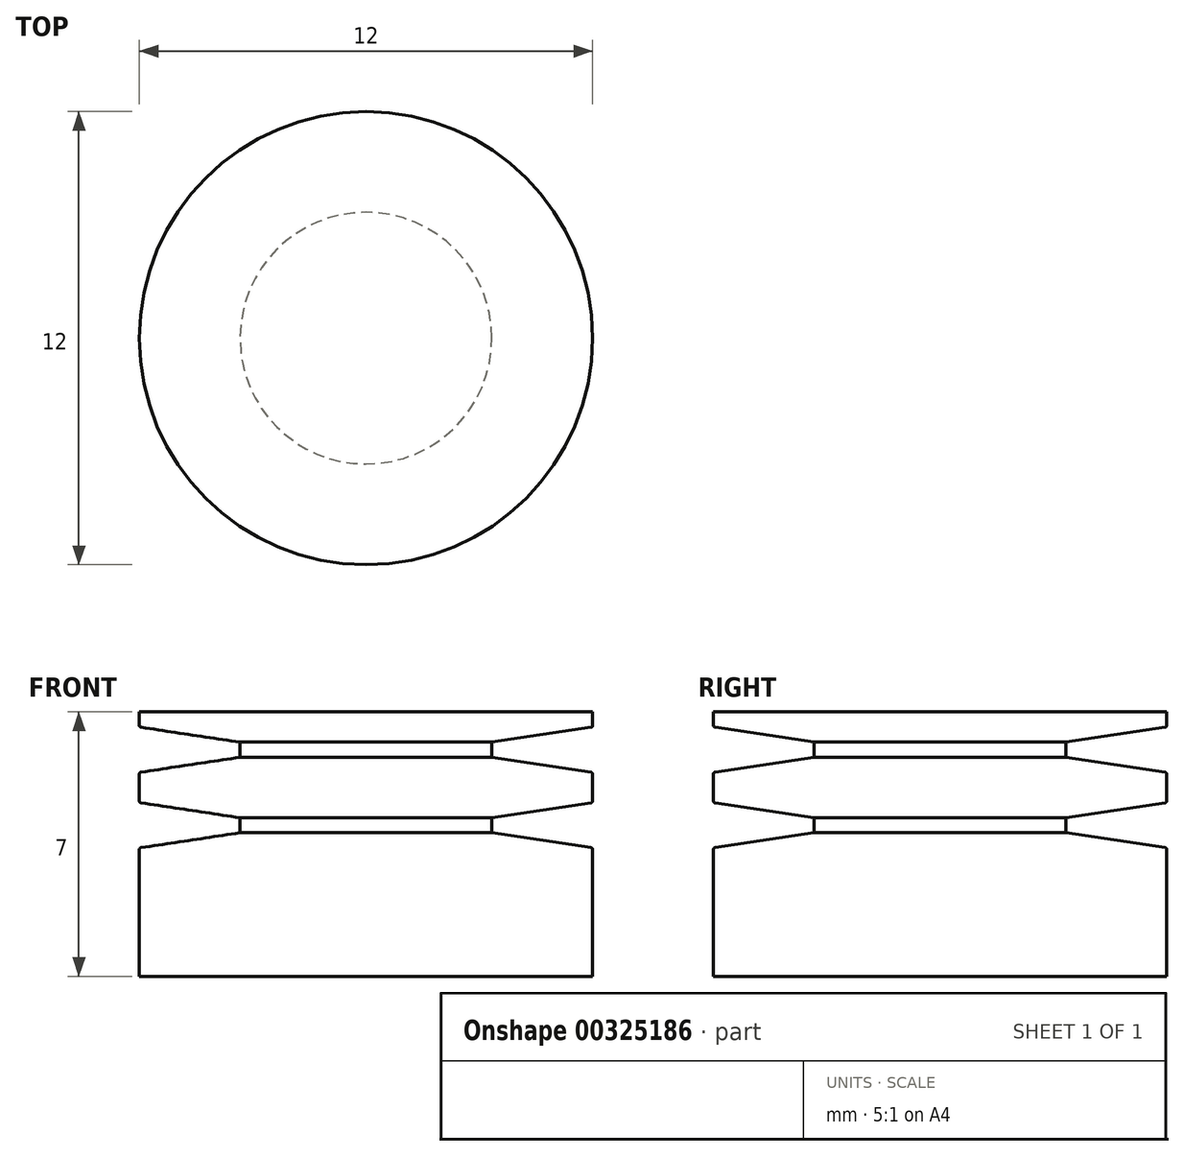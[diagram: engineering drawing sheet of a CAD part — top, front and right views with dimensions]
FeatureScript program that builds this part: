
annotation { "Feature Type Name" : "Feature", "Feature Type Description" : "" }
export const myFeature = defineFeature(function(context is Context, id is Id, definition is map)
    precondition{}
    {
        {
            var Q0;
            Q0=qCreatedBy(makeId("Front.planeOp"),FACE);
            var sketch = newSketch(context, id + "F0", { "sketchPlane" : qUnion([Q0])});
            skLineSegment(sketch, "E0.top", {"start": v(0, 3) * mm, "end": v(6, 3) * mm});
            skLineSegment(sketch, "E1", {"start": v(0, 3) * mm, "end": v(0, 4) * mm});
            skLineSegment(sketch, "E2", {"start": v(0, 4) * mm, "end": v(2, 4) * mm});
            skLineSegment(sketch, "E3", {"start": v(6, 3) * mm, "end": v(6, 3.36) * mm});
            skLineSegment(sketch, "E4", {"start": v(5.96, 3.4) * mm, "end": v(2, 4) * mm});
            skLineSegment(sketch, "E5", {"start": v(3.33, 4) * mm, "end": v(3.33, 3.8) * mm});
            skLineSegment(sketch, "E6", {"start": v(2, 4) * mm, "end": v(3.33, 4) * mm});
            skPoint(sketch, "E7.visualSharp", {"position": v(6, 3.4) * mm});
            skArc(sketch, "E7.filletArc", {"start": v(6, 3.36) * mm, "mid": v(5.99, 3.39) * mm, "end": v(5.96, 3.4) * mm});
            skSolve(sketch);
        }
        {
            var Q0;
            Q0=makeQuery(id+"F0.imprint","IMPRINT",FACE,{"disambiguationData":[TD([[makeQuery(id+"F0.imprint","IMPRINT",EDGE,{"derivedFrom":sQuery(id+"F0.wireOp",EDGE,"E0.top")}),1.0]])]});
            var Q1;
            {var subQ2=sQuery(id+"F0.wireOp",EDGE,"E5");Q1=makeQuery(id+"F0.imprint","IMPRINT",FACE,{"disambiguationData":[TD([[makeQuery(id+"F0.imprint","IMPRINT",EDGE,{"derivedFrom":subQ2}),-1.0]])]});}
            var Q2;
            Q2=sQuery(id+"F0.wireOp",EDGE,"E1");
            revolve(context, id + "F1", {"entities" : qUnion([Q0, Q1]), "axis" : qUnion([Q2]), "revolveType" : RevolveType.FULL});
        }
        {
            var Q0;
            Q0=makeQuery(id+"F1.opRevolve","SWEPT_BODY",BODY,{"disambiguationData":[OSD([sQuery(id+"F0.wireOp",EDGE,"E0.top"),sQuery(id+"F0.wireOp",EDGE,"E1"),sQuery(id+"F0.wireOp",EDGE,"E2"),sQuery(id+"F0.wireOp",EDGE,"E3"),sQuery(id+"F0.wireOp",EDGE,"E4"),sQuery(id+"F0.wireOp",EDGE,"E5"),sQuery(id+"F0.wireOp",EDGE,"E6")])]});
            var Q1;
            Q1=makeQuery(id+"F1.opRevolve","SWEPT_FACE",FACE,{"disambiguationData":[OSD([sQuery(id+"F0.wireOp",EDGE,"E2"),sQuery(id+"F0.wireOp",EDGE,"E6")])]});
            mirror(context, id + "F2", {"operationType" : NewBodyOperationType.ADD, "entities" : qUnion([Q0]), "mirrorPlane" : qUnion([Q1])});
        }
        {
            var Q0;
            Q0=makeQuery(id+"F1.opRevolve","SWEPT_BODY",BODY,{"disambiguationData":[OSD([sQuery(id+"F0.wireOp",EDGE,"E0.top"),sQuery(id+"F0.wireOp",EDGE,"E1"),sQuery(id+"F0.wireOp",EDGE,"E2"),sQuery(id+"F0.wireOp",EDGE,"E3"),sQuery(id+"F0.wireOp",EDGE,"E4"),sQuery(id+"F0.wireOp",EDGE,"E5"),sQuery(id+"F0.wireOp",EDGE,"E6")])]});
            var Q1;
            Q1=makeQuery(id+"F2.opPattern","COPY",FACE,{"derivedFrom":makeQuery(id+"F1.opRevolve","SWEPT_FACE",FACE,{"disambiguationData":[OSD([sQuery(id+"F0.wireOp",EDGE,"E0.top")])]}),"instanceName":"1"});
            mirror(context, id + "F3", {"operationType" : NewBodyOperationType.ADD, "entities" : qUnion([Q0]), "mirrorPlane" : qUnion([Q1])});
        }
        {
            var Q0;
            Q0=makeQuery(id+"F1.opRevolve","SWEPT_FACE",FACE,{"disambiguationData":[OSD([sQuery(id+"F0.wireOp",EDGE,"E0.top")])]});
            var Q1;
            Q1=qCreatedBy(makeId("Origin.pointOp"),VERTEX);
            extrude(context, id + "F4", {"entities" : qUnion([Q0]), "operationType" : NewBodyOperationType.ADD, "endBound" : BoundingType.UP_TO_VERTEX, "endBoundEntityVertex" : qUnion([Q1]), "depth" : 3 * mm});
        }
    });
